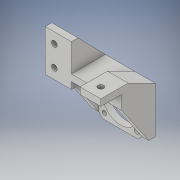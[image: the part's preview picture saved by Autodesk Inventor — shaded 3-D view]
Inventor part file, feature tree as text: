
AUTODESK INVENTOR PART (.ipt)
format: ipt  version: 2019 (Build 230136000, 136)  size: 156,672 bytes
history: native  units: in
note: dims shown in document units (in); Inventor stores cm internally (conversion verified against a paired STEP export)
features: other x3, plane x1
ambient origin geometry x8: Origin, YZ Plane, XZ Plane, XY Plane, X Axis, Y Axis, Z Axis, Center Point
bodies: Solid1 (feature_tree)
feature tree (4):
  other  "motorBracket.ipt"
  other  "Solid1::motorBracket.ipt"
  other  "TaggingFeature1"
  plane  "Work Plane1"
